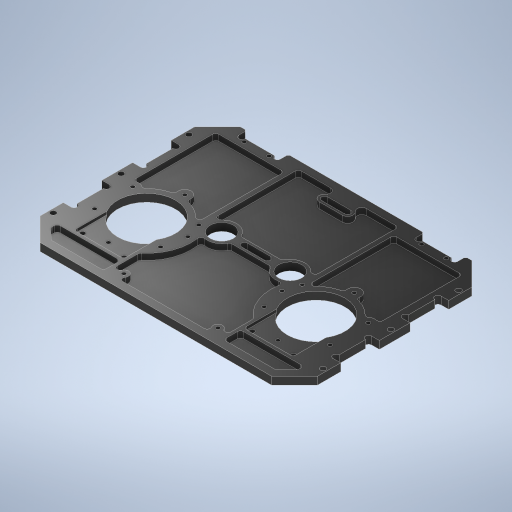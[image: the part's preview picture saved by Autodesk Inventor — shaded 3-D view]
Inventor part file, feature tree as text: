
AUTODESK INVENTOR PART (.ipt)
format: ipt  version: 2024.2 (Build 282272000, 272)  size: 865,280 bytes
history: native  units: mm
features: extrude x2, hole x2, sketch x1, mirror x1, chamfer x1
ambient origin geometry x8: Origin, YZ Plane, XZ Plane, XY Plane, X Axis, Y Axis, Z Axis, Center Point
bodies: Solid1 (feature_tree)
feature tree (7):
  sketch  "Sketch1"  dims[d0=130.0mm d1=180.0mm d2=37.5mm d4=60.0mm d6=360.0deg d8=58.0mm d9=49.5mm d10=43.0mm d11=32.0mm d12=27.0mm d13=27.0mm d21=5.0mm d22=0.05mm d23=20.0mm d25=25.0mm d27=5.0mm d28=0.0mm d29=2.0mm d30=0.0mm d31=2.459mm d32=6.0mm d33=4.0mm d34=2.0mm d35=90.0deg d36=8.0mm d37=20.594885mm d38=3.5mm d39=6.0mm d40=4.0mm d41=2.0mm d42=90.0deg d43=8.0mm d44=20.594885mm d45=3.1mm d46=6.0mm d47=4.0mm d48=2.0mm d49=90.0deg d50=8.0mm d51=20.594885mm d52=2.0mm d53=2.0mm d78=1.0mm d79=1.0mm d94=6.0mm d96=6.0mm d99=4.0mm d100=0.0mm d147=6.0mm d151=110.0mm d154=0.05mm d156=16.0mm d158=9.5mm d159=8.5mm d160=50.0mm d161=75.0mm d163=7.0mm d165=15.0mm d166=29.387501mm d167=5.0mm d168=6.0mm d172=2.0mm d174=2.0mm d175=2.0mm d176=9.0mm d184=15.0mm d186=45.0deg d187=48.0mm d188=140.0mm d191=5.0mm d195=3.0mm d202=5.0mm d206=4.0mm d207=15.0mm d208=1.5mm d209=41.5mm d211=45.0mm d214=2.0mm d216=3.0mm d217=11.9mm d218=25.0mm d219=16.0mm d220=0.8mm d221=1.0mm d223=5.0mm d224=4.0mm d225=5.0mm d227=5.0mm d228=0.1mm d229=5.0mm d230=115.0mm d231=1.0mm d232=2.0mm d233=45.0deg d66=1.0mm d67=1.0mm d68=1.0mm d69=0.15mm d70=0.25mm d71=0.375mm d72=14.3117mm d73=0.75mm d74=20.594885mm d75=0.0625mm d76=0.75mm d77=0.375mm d101=0.5mm d102=0.872665mm d121=0.5mm d122=0.872665mm d123=0.5mm d124=0.872665mm d234=0.872665mm]
  extrude  "Extrusion1"  Depth=180.0mm
  extrude  "Extrusion2"  Depth=1.0mm
  hole  "Phi3.5"  [1 undecoded]
  hole  "Phi3.1"  [1 undecoded]
  mirror  "Mirror1"
  chamfer  "Work Plane1"  Distance=49.5mm
note: 2 required parameter values undecoded (feature->parameter linkage not recoverable at this tier; creation-order binding heuristic only, values carry confidence <= 0.55)
